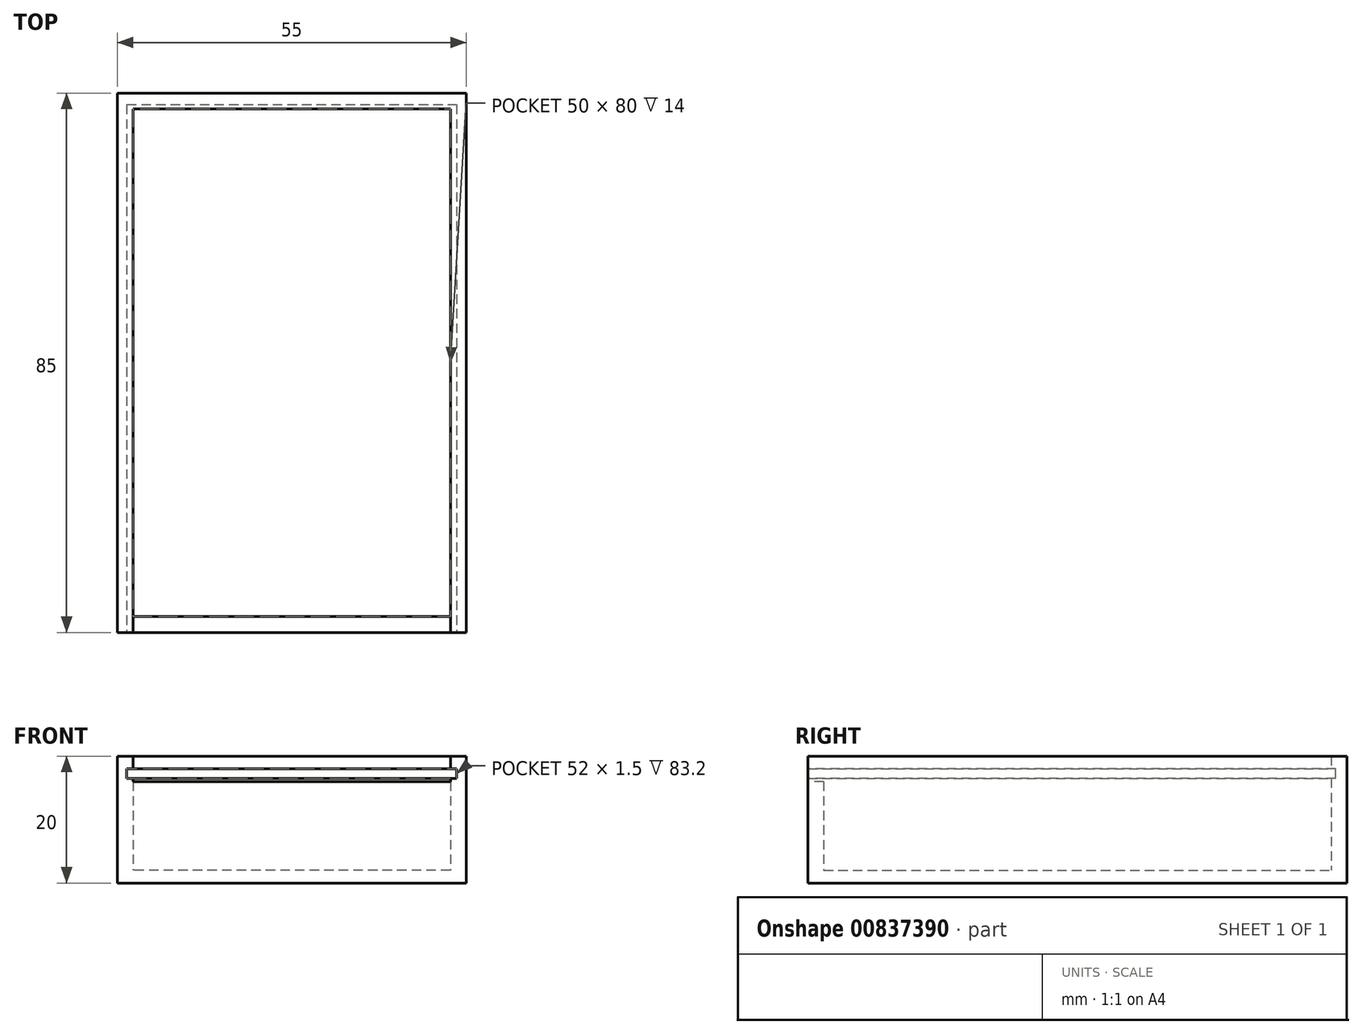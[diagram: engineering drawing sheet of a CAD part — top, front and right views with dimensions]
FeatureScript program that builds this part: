
annotation { "Feature Type Name" : "Feature", "Feature Type Description" : "" }
export const myFeature = defineFeature(function(context is Context, id is Id, definition is map)
    precondition{}
    {
        {
            var Q0;
            Q0=qCreatedBy(makeId("Top.planeOp"),FACE);
            var sketch = newSketch(context, id + "F0", { "sketchPlane" : qUnion([Q0])});
            skLineSegment(sketch, "E0.bottom", {"start": v(-25, 40) * mm, "end": v(25, 40) * mm});
            skLineSegment(sketch, "E0.top", {"start": v(-25, -40) * mm, "end": v(25, -40) * mm});
            skLineSegment(sketch, "E0.left", {"start": v(-25, 40) * mm, "end": v(-25, -40) * mm});
            skLineSegment(sketch, "E0.right", {"start": v(25, 40) * mm, "end": v(25, -40) * mm});
            skLineSegment(sketch, "E1.0", {"start": v(27.5, 42.5) * mm, "end": v(27.5, -42.5) * mm});
            skLineSegment(sketch, "E1.1", {"start": v(-27.5, 42.5) * mm, "end": v(27.5, 42.5) * mm});
            skLineSegment(sketch, "E1.2", {"start": v(-27.5, 42.5) * mm, "end": v(-27.5, -42.5) * mm});
            skLineSegment(sketch, "E1.3", {"start": v(-27.5, -42.5) * mm, "end": v(27.5, -42.5) * mm});
            skSolve(sketch);
        }
        {
            var Q0;
            Q0 = qSketchRegion(id + "F0", true);
            var Q1;
            Q1=makeQuery(id+"F0.imprint","IMPRINT",FACE,{"disambiguationData":[TD([[makeQuery(id+"F0.imprint","IMPRINT",EDGE,{"derivedFrom":sQuery(id+"F0.wireOp",EDGE,"E0.bottom")}),-1.0]])]});
            extrude(context, id + "F1", {"entities" : qUnion([Q0, Q1]), "depth" : 2 * mm, "offsetDistance" : 25 * mm});
        }
        {
            var Q0;
            Q0 = qSketchRegion(id + "F0", true);
            extrude(context, id + "F2", {"entities" : qUnion([Q0]), "operationType" : NewBodyOperationType.ADD, "depth" : 20 * mm, "offsetDistance" : 25 * mm});
        }
        {
            var Q0;
            {var subQ0=sQuery(id+"F0.wireOp",EDGE,"E1.3");Q0=makeQuery(id+"F2.boolean.opBoolean","MERGE",FACE,{"derivedFrom":[makeQuery(id+"F1.opExtrude","SWEPT_FACE",FACE,{"disambiguationData":[OSD([subQ0])]}),makeQuery(id+"F2.opExtrude","SWEPT_FACE",FACE,{"disambiguationData":[OSD([subQ0])]})]});}
            var sketch = newSketch(context, id + "F3", { "sketchPlane" : qUnion([Q0])});
            skLineSegment(sketch, "E2.bottom", {"start": v(-25, 20) * mm, "end": v(25, 20) * mm});
            skLineSegment(sketch, "E2.top", {"start": v(-25, 16) * mm, "end": v(25, 16) * mm});
            skLineSegment(sketch, "E2.left", {"start": v(-25, 20) * mm, "end": v(-25, 16) * mm});
            skLineSegment(sketch, "E2.right", {"start": v(25, 20) * mm, "end": v(25, 16) * mm});
            skSolve(sketch);
        }
        {
            var Q0;
            Q0=makeQuery(id+"F3.imprint","IMPRINT",FACE,{"disambiguationData":[TD([[makeQuery(id+"F3.imprint","IMPRINT",EDGE,{"derivedFrom":sQuery(id+"F3.wireOp",EDGE,"E2.bottom")}),-1.0]])]});
            var Q1;
            Q1=makeQuery(id+"F2.opExtrude","SWEPT_FACE",FACE,{"disambiguationData":[OSD([sQuery(id+"F0.wireOp",EDGE,"E0.bottom")])]});
            extrude(context, id + "F4", {"entities" : qUnion([Q0]), "operationType" : NewBodyOperationType.REMOVE, "endBound" : BoundingType.UP_TO_SURFACE, "oppositeDirection" : true, "depth" : 25 * mm, "endBoundEntityFace" : qUnion([Q1]), "offsetDistance" : 25 * mm});
        }
        {
            var Q0;
            {var subQ0=sQuery(id+"F0.wireOp",EDGE,"E1.3");Q0=makeQuery(id+"F2.boolean.opBoolean","MERGE",FACE,{"derivedFrom":[makeQuery(id+"F1.opExtrude","SWEPT_FACE",FACE,{"disambiguationData":[OSD([subQ0])]}),makeQuery(id+"F2.opExtrude","SWEPT_FACE",FACE,{"disambiguationData":[OSD([subQ0])]})]});}
            var sketch = newSketch(context, id + "F5", { "sketchPlane" : qUnion([Q0])});
            skPoint(sketch, "E3.oppositeSnap0", {"position": v(25, 18) * mm});
            skLineSegment(sketch, "E3.bottom", {"start": v(-26, 16.5) * mm, "end": v(26, 16.5) * mm});
            skLineSegment(sketch, "E3.top", {"start": v(-26, 18) * mm, "end": v(26, 18) * mm});
            skLineSegment(sketch, "E3.left", {"start": v(-26, 16.5) * mm, "end": v(-26, 18) * mm});
            skLineSegment(sketch, "E3.right", {"start": v(26, 16.5) * mm, "end": v(26, 18) * mm});
            skSolve(sketch);
        }
        {
            var Q0;
            {var subQ0=sQuery(id+"F5.wireOp",EDGE,"E3.bottom");var subQ1=makeQuery(id+"F4.boolean.opBoolean","COPY",EDGE,{"derivedFrom":makeQuery(id+"F4.opExtrude","CAP_EDGE",EDGE,{"disambiguationData":[OSD([sQuery(id+"F3.wireOp",EDGE,"E2.left")])],"isStart":true})});var subQ2=makeQuery(id+"F5.imprint","INTERSECT",VERTEX,{"derivedFrom":[subQ1,subQ0]});Q0=makeQuery(id+"F5.imprint","IMPRINT",FACE,{"disambiguationData":[TD([[makeQuery(id+"F5.imprint","IMPRINT",EDGE,{"disambiguationData":[TD([[subQ2,-1.0]])],"derivedFrom":subQ0}),1.0]])]});}
            var Q1;
            {var subQ0=sQuery(id+"F5.wireOp",EDGE,"E3.left");Q1=makeQuery(id+"F5.imprint","IMPRINT",FACE,{"disambiguationData":[TD([[makeQuery(id+"F5.imprint","IMPRINT",EDGE,{"derivedFrom":subQ0}),-1.0]])]});}
            var Q2;
            {var subQ0=sQuery(id+"F5.wireOp",EDGE,"E3.right");Q2=makeQuery(id+"F5.imprint","IMPRINT",FACE,{"disambiguationData":[TD([[makeQuery(id+"F5.imprint","IMPRINT",EDGE,{"derivedFrom":subQ0}),1.0]])]});}
            extrude(context, id + "F6", {"entities" : qUnion([Q0, Q1, Q2]), "operationType" : NewBodyOperationType.REMOVE, "oppositeDirection" : true, "depth" : 83.2 * mm, "offsetDistance" : 25 * mm});
        }
    });
